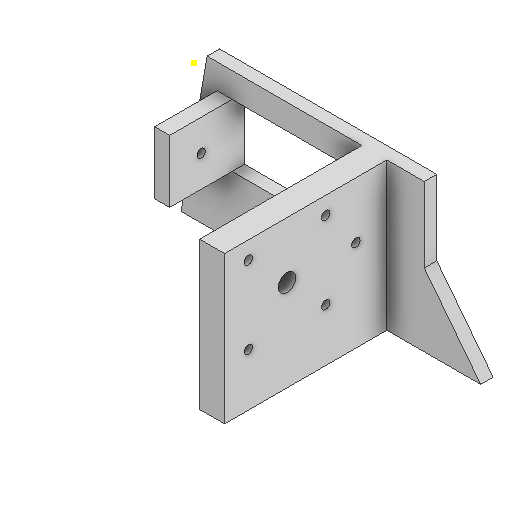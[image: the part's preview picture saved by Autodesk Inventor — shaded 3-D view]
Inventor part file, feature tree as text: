
AUTODESK INVENTOR PART (.ipt)
format: ipt  version: 2025.1 (Build 291241000, 241)  size: 201,728 bytes
history: native  units: mm
features: sketch x10, extrude x8, hole x3, other x1
ambient origin geometry x8: Origin, YZ Plane, XZ Plane, XY Plane, X Axis, Y Axis, Z Axis, Center Point
bodies: Body1 (feature_tree)
feature tree (22):
  other  "Bryła1"
  sketch  "Szkic1"
  extrude  "Wyciągnięcie proste1"  Depth=120.0mm
  extrude  "Wyciągnięcie proste2"  Depth=60.0mm
  extrude  "Wyciągnięcie proste3"  Depth=13.962634mm
  sketch  "Szkic2"
  extrude  "Wyciągnięcie proste4"  Depth=60.0mm
  extrude  "Wyciągnięcie proste5"  TaperAngle=0.0deg  [1 undecoded]
  extrude  "Wyciągnięcie proste6"  Depth=50.0mm
  hole  "Otwór1"  [1 undecoded]
  extrude  "Wyciągnięcie proste7"  Depth=10.0mm
  extrude  "Wyciągnięcie proste8"  Depth=10.0mm
  hole  "Otwór2"  [1 undecoded]
  hole  "Otwór3"  [1 undecoded]
  sketch  "Szkic3"
  sketch  "Szkic4"
  sketch  "Szkic5"
  sketch  "Szkic6"
  sketch  "Szkic7"
  sketch  "Szkic8"
  sketch  "Szkic9"
  sketch  "Szkic10"
note: 4 required parameter values undecoded (feature->parameter linkage not recoverable at this tier; creation-order binding heuristic only, values carry confidence <= 0.55)
